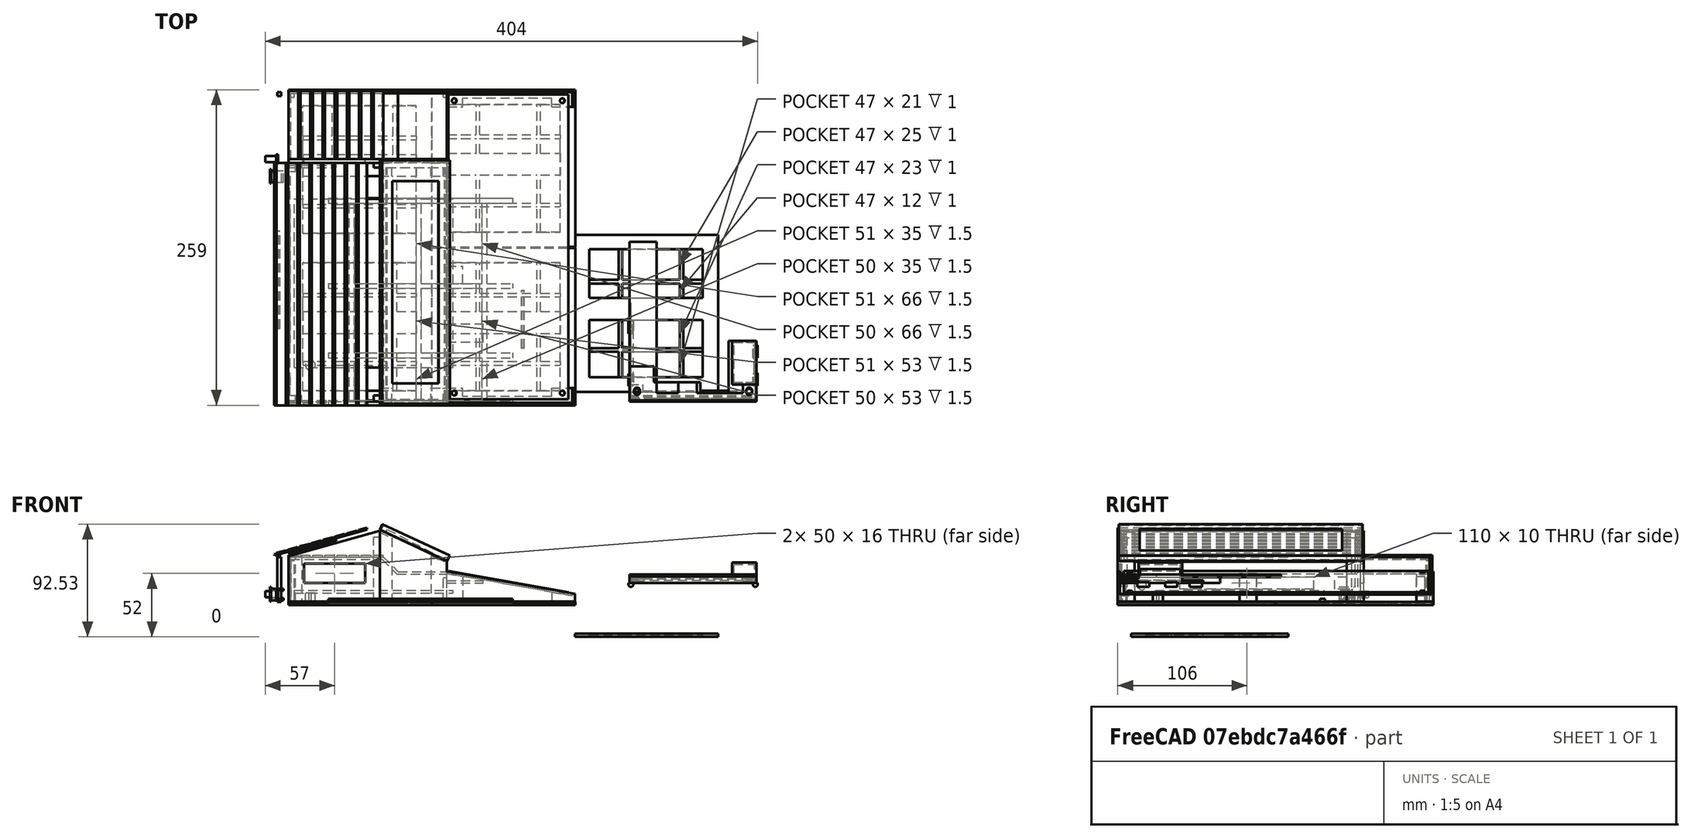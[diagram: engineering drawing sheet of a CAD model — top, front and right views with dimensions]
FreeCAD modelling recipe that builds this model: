
FCSTD DOCUMENT  (FreeCAD 0.20R29603 (Git))
Label: megav1
License: All rights reserved
LicenseURL: http://en.wikipedia.org/wiki/All_rights_reserved
objects: Part::Box×164, Part::Cut×62, Part::MultiFuse×26, Part::Cylinder×20, App::DocumentObjectGroup×8, Part::FeaturePython×1
note: 273 computed .brp shape members not serialized (recipe doc carries the construction recipe); baked Part::Feature solids carry a one-line shape summary decoded from their .brp

FEATURE [Part::Box] Box  label="5x50Keyboard"
  AttacherType = Attacher::AttachEngine3D
  Height = 2
  Length = 100
  Width = 250
FEATURE [Part::Box] Box001  label="MainBoardPCB"
  AttacherType = Attacher::AttachEngine3D
  Height = 2
  Length = 130
  Placement = pos=(-125,28,-8) rot=(0,0,1;0rad)
  Width = 138.5
FEATURE [Part::Box] Box002  label="4x40lcd"
  AttacherType = Attacher::AttachEngine3D
  Height = 2
  Length = 54
  Placement = pos=(-56,2,30) rot=(0,1,0;0.296706rad)
  Width = 190
FEATURE [Part::Box] Box050  label="Cube028"
  AttacherType = Attacher::AttachEngine3D
  Height = 9.5
  Length = 11
  Placement = pos=(0,0,35) rot=(0,0,1;0rad)
  Width = 9.5
FEATURE [Part::Box] Box051  label="Cube029"
  AttacherType = Attacher::AttachEngine3D
  Height = 12
  Length = 1
  Placement = pos=(0,-1,34) rot=(0,0,1;0rad)
  Width = 12
FEATURE [Part::Box] Box052  label="Cube030"
  AttacherType = Attacher::AttachEngine3D
  Height = 7.5
  Length = 4.5
  Placement = pos=(5,-1,36) rot=(0,0,1;0rad)
  Width = 13
FEATURE [Part::Box] Box053  label="Cube031"
  AttacherType = Attacher::AttachEngine3D
  Height = 6
  Length = 4.5
  Placement = pos=(9,-1,36.75) rot=(0,0,1;0rad)
  Width = 13
FEATURE [Part::Cylinder] Cylinder008
  Angle = 360
  AttacherType = Attacher::AttachEngine3D
  FirstAngle = 0
  Height = 9
  Placement = pos=(-1,5,40) rot=(0,1,0;1.5708rad)
  Radius = 3
  SecondAngle = 0
FEATURE [Part::MultiFuse] Fusion010
  Shapes = -> [Box050,Box051]
FEATURE [Part::Cut] Cut016
  Base = -> Fusion010
  Tool = -> Cylinder008
FEATURE [Part::Cut] Cut017
  Base = -> Cut016
  Tool = -> Box052
FEATURE [Part::Cut] Cut018
  Base = -> Cut017
  Placement = pos=(-145,180,-49) rot=(0,0,1;0rad)
  Tool = -> Box053
FEATURE [App::DocumentObjectGroup] Group007  label="resetbutton-case"
  Group = -> [Cut018]
FEATURE [Part::Box] Box054  label="Cube002"
  AttacherType = Attacher::AttachEngine3D
  Height = 37
  Length = 1.5
  Placement = pos=(0,0,-10) rot=(0,0,1;0rad)
  Width = 194
FEATURE [Part::Box] Box004  label="Cube003"
  AttacherType = Attacher::AttachEngine3D
  Height = 10
  Length = 10
  Placement = pos=(-3,48,0) rot=(0,0,1;0rad)
  Width = 110
FEATURE [Part::Box] Box021  label="reset"
  AttacherType = Attacher::AttachEngine3D
  Height = 10
  Length = 10
  Placement = pos=(-2,175,0) rot=(0,0,1;0rad)
  Width = 10
FEATURE [Part::Box] Box025  label="Cube004"
  AttacherType = Attacher::AttachEngine3D
  Height = 37
  Length = 5
  Placement = pos=(1,0,-8.5) rot=(0,0,1;0rad)
  Width = 5
FEATURE [Part::Box] Box026  label="Cube005"
  AttacherType = Attacher::AttachEngine3D
  Height = 37
  Length = 5
  Placement = pos=(1,189,-8.5) rot=(0,0,1;0rad)
  Width = 5
FEATURE [Part::Cylinder] Cylinder004  label="pwrjack"
  Angle = 360
  AttacherType = Attacher::AttachEngine3D
  FirstAngle = 0
  Height = 10
  Placement = pos=(-3,17,3) rot=(0,1,0;1.5708rad)
  Radius = 3.5
  SecondAngle = 0
FEATURE [Part::Cut] Cut003
  Base = -> Box054
  Tool = -> Cylinder004
FEATURE [Part::Cut] Cut
  Base = -> Cut003
  Tool = -> Box004
FEATURE [Part::Cut] Cut006
  Base = -> Cut
  Placement = pos=(0,0,1.5) rot=(0,0,1;0rad)
  Tool = -> Box021
FEATURE [Part::MultiFuse] Fusion011
  Placement = pos=(-130,0,-6.5) rot=(0,0,1;0rad)
  Shapes = -> [Box025,Cut006,Box026]
FEATURE [App::DocumentObjectGroup] Group002  label="Back"
  Group = -> [Fusion011]
FEATURE [Part::Box] Box055  label="Cube032"
  AttacherType = Attacher::AttachEngine3D
  Height = 5.5
  Length = 1.5
  Placement = pos=(7,1,37) rot=(0,0,1;0rad)
  Width = 8
FEATURE [Part::Cylinder] Cylinder009
  Angle = 360
  AttacherType = Attacher::AttachEngine3D
  FirstAngle = 0
  Height = 10
  Placement = pos=(-2,5,40) rot=(0,1,0;1.5708rad)
  Radius = 2.5
  SecondAngle = 0
FEATURE [Part::MultiFuse] Fusion012
  Placement = pos=(-147,194,-49) rot=(0,0,1;0rad)
  Shapes = -> [Cylinder009,Box055]
FEATURE [App::DocumentObjectGroup] Group008  label="resetbutton"
  Group = -> [Fusion012]
FEATURE [Part::Box] Box056  label="base"
  AttacherType = Attacher::AttachEngine3D
  Height = 1.5
  Length = 235
  Placement = pos=(-25,0,-10) rot=(1,0,0;0rad)
  Width = 259
FEATURE [Part::Box] Box027  label="Cube006"
  AttacherType = Attacher::AttachEngine3D
  Height = 4
  Length = 151
  Placement = pos=(8,0,-9) rot=(0,0,1;0rad)
  Width = 4
FEATURE [Part::Box] Box028  label="Cube007"
  AttacherType = Attacher::AttachEngine3D
  Height = 4
  Length = 151
  Placement = pos=(8,166,-9) rot=(0,0,1;0rad)
  Width = 4
FEATURE [Part::Box] Box029  label="Face003"
  AttacherType = Attacher::AttachEngine3D
  Height = 55
  Length = 2
  Placement = pos=(169.2,0,-11) rot=(0,-1,0;0.261799rad)
  Width = 254
FEATURE [Part::Box] Box036  label="Cube014"
  AttacherType = Attacher::AttachEngine3D
  Height = 2
  Length = 151
  Placement = pos=(8,96,-9) rot=(0,0,1;0rad)
  Width = 4
FEATURE [Part::Box] Box037  label="Cube015"
  AttacherType = Attacher::AttachEngine3D
  Height = 2
  Length = 151
  Placement = pos=(8,39,-9) rot=(0,0,1;0rad)
  Width = 4
FEATURE [Part::Box] Box038  label="Cube016"
  AttacherType = Attacher::AttachEngine3D
  Height = 2
  Length = 170
  Placement = pos=(29,0,-9) rot=(0,0,1;1.5708rad)
  Width = 4
FEATURE [Part::Box] Box039  label="Cube017"
  AttacherType = Attacher::AttachEngine3D
  Height = 2
  Length = 170
  Placement = pos=(84,0,-9) rot=(0,0,1;1.5708rad)
  Width = 4
FEATURE [Part::Box] Box040  label="Cube018"
  AttacherType = Attacher::AttachEngine3D
  Height = 2
  Length = 170
  Placement = pos=(138,0,-9) rot=(0,0,1;1.5708rad)
  Width = 4
FEATURE [Part::Cylinder] Cylinder007
  Angle = 360
  AttacherType = Attacher::AttachEngine3D
  FirstAngle = 0
  Height = 47
  Placement = pos=(167.4,94,-8.1) rot=(1,0,0;1.5708rad)
  Radius = 1
  SecondAngle = 0
FEATURE [Part::MultiFuse] Fusion005
  Shapes = -> [Box027,Box028]
FEATURE [Part::Cut] Cut009
  Base = -> Fusion005
  Tool = -> Box029
FEATURE [Part::MultiFuse] Fusion006
  Placement = pos=(-105,-3,-8) rot=(0,0,1;0rad)
  Refine = true
  Shapes = -> [Cut009,Cylinder007,Box036,Box037,Box038,Box039,Box040,Box056]
FEATURE [App::DocumentObjectGroup] Group009  label="CaseBaseold"
  Group = -> [Fusion006]
FEATURE [Part::FeaturePython] Tube002  label="PCBFoot"  # WARN: FeaturePython — macro-defined, semantics opaque (R4)
  AttacherType = Attacher::AttachEngine3D
  Height = 7
  InnerRadius = 1
  OuterRadius = 4
  Placement = pos=(-112,30,-15) rot=(0,0,1;0rad)
FEATURE [Part::Cylinder] Cylinder010
  Angle = 360
  AttacherType = Attacher::AttachEngine3D
  FirstAngle = 0
  Height = 20
  Placement = pos=(5,5,-2) rot=(0,0,1;0rad)
  Radius = 2
  SecondAngle = 0
FEATURE [Part::Cylinder] Cylinder011
  Angle = 360
  AttacherType = Attacher::AttachEngine3D
  FirstAngle = 0
  Height = 20
  Placement = pos=(5,245,-2) rot=(0,0,1;0rad)
  Radius = 2
  SecondAngle = 0
FEATURE [Part::Cylinder] Cylinder012
  Angle = 360
  AttacherType = Attacher::AttachEngine3D
  FirstAngle = 0
  Height = 20
  Placement = pos=(95,245,-2) rot=(0,0,1;0rad)
  Radius = 2
  SecondAngle = 0
FEATURE [Part::Cylinder] Cylinder013
  Angle = 360
  AttacherType = Attacher::AttachEngine3D
  FirstAngle = 0
  Height = 20
  Placement = pos=(95,5,-2) rot=(0,0,1;0rad)
  Radius = 2
  SecondAngle = 0
FEATURE [Part::Cut] Cut019
  Base = -> Box
  Tool = -> Cylinder010
FEATURE [Part::Cut] Cut020
  Base = -> Cut019
  Tool = -> Cylinder011
FEATURE [Part::Cut] Cut021
  Base = -> Cut020
  Tool = -> Cylinder012
FEATURE [Part::Cut] Cut022
  Base = -> Cut021
  Placement = pos=(0,2,5) rot=(0,0,1;0rad)
  Tool = -> Cylinder013
FEATURE [Part::MultiFuse] Fusion
  Placement = pos=(0,0,3) rot=(0,1,0;0.174533rad)
  Shapes = -> [Box002,Cut022]
FEATURE [App::DocumentObjectGroup] Group  label="PCB"
  Group = -> [Box001,Fusion]
FEATURE [Part::Box] Box057  label="pil1"
  AttacherType = Attacher::AttachEngine3D
  Height = 25
  Length = 105
  Placement = pos=(0,-2,-15) rot=(0,0,1;0rad)
  Width = 14
FEATURE [Part::Box] Box058  label="Cube033"
  AttacherType = Attacher::AttachEngine3D
  Height = 41
  Length = 116
  Placement = pos=(-1,-5,8) rot=(0,1,0;0.174533rad)
  Width = 17
FEATURE [Part::Cut] Cut023  label="leftpailslanted"
  Base = -> Box057
  Placement = pos=(0,-1,0) rot=(0,0,1;0rad)
  Tool = -> Box058
FEATURE [Part::Box] Box059  label="pil002"
  AttacherType = Attacher::AttachEngine3D
  Height = 25
  Length = 105
  Placement = pos=(0,-2,-15) rot=(0,0,1;0rad)
  Width = 2
FEATURE [Part::Box] Box060  label="Cube034"
  AttacherType = Attacher::AttachEngine3D
  Height = 41
  Length = 116
  Placement = pos=(-1,-5,8) rot=(0,1,0;0.174533rad)
  Width = 17
FEATURE [Part::Cut] Cut024  label="leftpailslanted001"
  Base = -> Box059
  Placement = pos=(0,-1,2) rot=(0,0,1;0rad)
  Tool = -> Box060
FEATURE [Part::Box] Box061  label="leftpilstop"
  AttacherType = Attacher::AttachEngine3D
  Height = 6
  Length = 2
  Placement = pos=(103,-3,-15) rot=(0,0,1;0rad)
  Width = 14
FEATURE [Part::Box] Box062  label="leftpilsfillremove"
  AttacherType = Attacher::AttachEngine3D
  Height = 27
  Length = 73
  Placement = pos=(13,4,-20) rot=(0,0,1;0rad)
  Width = 10
FEATURE [Part::Box] Box063  label="pil003"
  AttacherType = Attacher::AttachEngine3D
  Height = 25
  Length = 105
  Placement = pos=(0,-2,-15) rot=(0,0,1;0rad)
  Width = 14
FEATURE [Part::Box] Box064  label="Cube035"
  AttacherType = Attacher::AttachEngine3D
  Height = 41
  Length = 116
  Placement = pos=(-1,-5,8) rot=(0,1,0;0.174533rad)
  Width = 17
FEATURE [Part::Cut] Cut025  label="rightpailslanted001"
  Base = -> Box063
  Placement = pos=(0,-1,0) rot=(0,0,1;0rad)
  Tool = -> Box064
FEATURE [Part::Box] Box065  label="pil004"
  AttacherType = Attacher::AttachEngine3D
  Height = 25
  Length = 105
  Placement = pos=(0,-2,-15) rot=(0,0,1;0rad)
  Width = 2
FEATURE [Part::Box] Box066  label="Cube036"
  AttacherType = Attacher::AttachEngine3D
  Height = 41
  Length = 116
  Placement = pos=(-1,-5,8) rot=(0,1,0;0.174533rad)
  Width = 17
FEATURE [Part::Cut] Cut026  label="rightpailslanted002"
  Base = -> Box065
  Placement = pos=(0,11,2) rot=(0,0,1;0rad)
  Tool = -> Box066
FEATURE [Part::Box] Box067  label="rightpilstop001"
  AttacherType = Attacher::AttachEngine3D
  Height = 6
  Length = 2
  Placement = pos=(103,-3,-15) rot=(0,0,1;0rad)
  Width = 14
FEATURE [Part::Box] Box068  label="rightpilsfillremove001"
  AttacherType = Attacher::AttachEngine3D
  Height = 27
  Length = 73
  Placement = pos=(13,-6,-20) rot=(0,0,1;0rad)
  Width = 10
FEATURE [Part::MultiFuse] Fusion013
  Shapes = -> [Cut023,Cut024,Box061]
FEATURE [Part::Cut] Cut027  label="LeftPillar"
  Base = -> Fusion013
  Tool = -> Box062
FEATURE [Part::MultiFuse] Fusion014
  Shapes = -> [Cut025,Cut026,Box067]
FEATURE [Part::Cut] Cut028  label="keyboardrightpillar"
  Base = -> Fusion014
  Placement = pos=(0,245,0) rot=(0,0,1;0rad)
  Tool = -> Box068
FEATURE [Part::Box] Box069  label="lcdpillar"
  AttacherType = Attacher::AttachEngine3D
  Height = 58
  Length = 55
  Placement = pos=(-55,-3,-15) rot=(0,0,1;0rad)
  Width = 14
FEATURE [Part::Box] Box070  label="lcdpillar001slant"
  AttacherType = Attacher::AttachEngine3D
  Height = 58
  Length = 78
  Placement = pos=(-64,-6,48) rot=(0,1,0;0.436332rad)
  Width = 18
FEATURE [Part::Box] Box071  label="lcdpillar001slant001edge"
  AttacherType = Attacher::AttachEngine3D
  Height = 58
  Length = 78
  Placement = pos=(-64,-1,46) rot=(0,1,0;0.436332rad)
  Width = 18
FEATURE [Part::Cut] Cut029
  Base = -> Box069
  Tool = -> Box070
FEATURE [Part::Cut] Cut030
  Base = -> Cut029
  Tool = -> Box071
FEATURE [Part::Box] Box072  label="lcdstopleft"
  AttacherType = Attacher::AttachEngine3D
  Height = 9
  Length = 3
  Placement = pos=(-3,-3,10) rot=(0,0,1;0rad)
  Width = 14
FEATURE [Part::Box] Box073  label="lcdremove"
  AttacherType = Attacher::AttachEngine3D
  Height = 63
  Length = 32
  Placement = pos=(-45,-1,-17) rot=(0,0,1;0rad)
  Width = 17
FEATURE [Part::MultiFuse] Fusion015
  Shapes = -> [Cut030,Box072]
FEATURE [Part::Cut] Cut031  label="leftlcdpillar"
  Base = -> Fusion015
  Tool = -> Box073
FEATURE [Part::Box] Box080  label="lcdpillar002"
  AttacherType = Attacher::AttachEngine3D
  Height = 58
  Length = 55
  Placement = pos=(-55,-3,-15) rot=(0,0,1;0rad)
  Width = 14
FEATURE [Part::Box] Box081  label="lcdpillar001slant002"
  AttacherType = Attacher::AttachEngine3D
  Height = 58
  Length = 78
  Placement = pos=(-64,-6,48) rot=(0,1,0;0.436332rad)
  Width = 18
FEATURE [Part::Box] Box082  label="lcdpillar001slant001edge002"
  AttacherType = Attacher::AttachEngine3D
  Height = 58
  Length = 78
  Placement = pos=(-64,-10,46) rot=(0,1,0;0.436332rad)
  Width = 18
FEATURE [Part::Box] Box084  label="lcdremove002"
  AttacherType = Attacher::AttachEngine3D
  Height = 63
  Length = 32
  Placement = pos=(-45,-9,-17) rot=(0,0,1;0rad)
  Width = 17
FEATURE [Part::Cut] Cut035
  Base = -> Box080
  Tool = -> Box081
FEATURE [Part::Cut] Cut036
  Base = -> Cut035
  Tool = -> Box082
FEATURE [Part::MultiFuse] Fusion019  label="keyboardlcdleftpillar"
  Shapes = -> [Cut027,Cut031]
FEATURE [Part::Box] Box090  label="extcartslot"
  AttacherType = Attacher::AttachEngine3D
  Height = 61
  Length = 75
  Placement = pos=(-130,-3,-15) rot=(0,0,1;0rad)
  Width = 3
FEATURE [Part::Box] Box091  label="Cube039"
  AttacherType = Attacher::AttachEngine3D
  Height = 41
  Length = 107
  Placement = pos=(-150,-8,16.5) rot=(0,-1,0;0.272271rad)
  Width = 10
FEATURE [Part::Cut] Cut041
  Base = -> Box090
  Tool = -> Box091
FEATURE [Part::Box] Box092  label="Cube040"
  AttacherType = Attacher::AttachEngine3D
  Height = 53
  Length = 5
  Placement = pos=(-60,0,-15) rot=(0,0,1;0rad)
  Width = 5
FEATURE [Part::Box] Box093  label="Cube041"
  AttacherType = Attacher::AttachEngine3D
  Height = 37
  Length = 5
  Placement = pos=(-124,0,-15) rot=(0,0,1;0rad)
  Width = 5
FEATURE [Part::MultiFuse] Fusion021  label="LeftExtCartSlot"
  Shapes = -> [Cut041,Box092,Box093]
FEATURE [Part::Box] Box094  label="extcartslot001"
  AttacherType = Attacher::AttachEngine3D
  Height = 61
  Length = 75
  Placement = pos=(-130,-3,-15) rot=(0,0,1;0rad)
  Width = 3
FEATURE [Part::Box] Box095  label="Cube042"
  AttacherType = Attacher::AttachEngine3D
  Height = 41
  Length = 107
  Placement = pos=(-150,-8,16.5) rot=(0,-1,0;0.272271rad)
  Width = 10
FEATURE [Part::Box] Box096  label="Cube043"
  AttacherType = Attacher::AttachEngine3D
  Height = 53
  Length = 5
  Placement = pos=(-60,-7,-15) rot=(0,0,1;0rad)
  Width = 5
FEATURE [Part::Box] Box097  label="Cube044"
  AttacherType = Attacher::AttachEngine3D
  Height = 37
  Length = 5
  Placement = pos=(-124,-7,-15) rot=(0,0,1;0rad)
  Width = 5
FEATURE [Part::Cut] Cut042
  Base = -> Box094
  Tool = -> Box095
FEATURE [Part::MultiFuse] Fusion022  label="RightExtCartSlot001"
  Placement = pos=(0,209.01,0) rot=(0,0,1;0rad)
  Shapes = -> [Cut042,Box096,Box097]
FEATURE [Part::Box] Box098  label="Lid"
  AttacherType = Attacher::AttachEngine3D
  Height = 1.5
  Length = 79
  Placement = pos=(-130,-3,22) rot=(0,1,0;0rad)
  Width = 199
FEATURE [Part::Box] Box099  label="LidRib1"
  AttacherType = Attacher::AttachEngine3D
  Height = 1
  Length = 2
  Placement = pos=(-130,-3,61) rot=(0,-1,0;0rad)
  Width = 199
FEATURE [Part::Box] Box100  label="LidRib002"
  AttacherType = Attacher::AttachEngine3D
  Height = 1
  Length = 2
  Placement = pos=(-120,-3,61) rot=(0,-1,0;0rad)
  Width = 199
FEATURE [Part::Box] Box101  label="LidRib003"
  AttacherType = Attacher::AttachEngine3D
  Height = 1
  Length = 2
  Placement = pos=(-110,-3,61) rot=(0,-1,0;0rad)
  Width = 199
FEATURE [Part::Box] Box102  label="LidRib004"
  AttacherType = Attacher::AttachEngine3D
  Height = 1
  Length = 2
  Placement = pos=(-100,-3,61) rot=(0,-1,0;0rad)
  Width = 199
FEATURE [Part::Box] Box103  label="LidRib005"
  AttacherType = Attacher::AttachEngine3D
  Height = 1
  Length = 2
  Placement = pos=(-90,-3,61) rot=(0,-1,0;0rad)
  Width = 199
FEATURE [Part::Box] Box104  label="LidRib006"
  AttacherType = Attacher::AttachEngine3D
  Height = 1
  Length = 2
  Placement = pos=(-80,-3,61) rot=(0,-1,0;0rad)
  Width = 199
FEATURE [Part::Box] Box105  label="LidRib007"
  AttacherType = Attacher::AttachEngine3D
  Height = 1
  Length = 2
  Placement = pos=(-70,-3,61) rot=(0,-1,0;0rad)
  Width = 199
FEATURE [Part::Box] Box106  label="LidRib008"
  AttacherType = Attacher::AttachEngine3D
  Height = 1
  Length = 2
  Placement = pos=(-60,-3,61) rot=(0,-1,0;0rad)
  Width = 199
FEATURE [Part::Box] Box107  label="Cube045"
  AttacherType = Attacher::AttachEngine3D
  Height = 2
  Length = 40
  Placement = pos=(-118,-1,20) rot=(0,0,1;0rad)
  Width = 2
FEATURE [Part::Box] Box108  label="Cube046"
  AttacherType = Attacher::AttachEngine3D
  Height = 2
  Length = 40
  Placement = pos=(-118,192,20) rot=(0,0,1;0rad)
  Width = 2
FEATURE [Part::Box] Box109  label="Cube047"
  AttacherType = Attacher::AttachEngine3D
  Height = 2
  Length = 2
  Placement = pos=(-128,60,20) rot=(0,0,1;0rad)
  Width = 80
FEATURE [Part::MultiFuse] Fusion023  label="Lid001"
  Placement = pos=(0,0,38) rot=(0,1,0;0rad)
  Shapes = -> [Box098,Box107,Box108,Box109]
FEATURE [Part::Cut] Cut043
  Base = -> Fusion023
  Tool = -> Box099
FEATURE [Part::Cut] Cut044
  Base = -> Cut043
  Tool = -> Box100
FEATURE [Part::Cut] Cut045
  Base = -> Cut044
  Tool = -> Box101
FEATURE [Part::Cut] Cut046
  Base = -> Cut045
  Tool = -> Box102
FEATURE [Part::Cut] Cut047
  Base = -> Cut046
  Tool = -> Box103
FEATURE [Part::Cut] Cut048
  Base = -> Cut047
  Tool = -> Box104
FEATURE [Part::Cut] Cut049
  Base = -> Cut048
  Tool = -> Box105
FEATURE [Part::Cut] Cut050  label="Lid002"
  Base = -> Cut049
  Placement = pos=(0,0,0) rot=(0,-1,0;0.272271rad)
  Tool = -> Box106
FEATURE [Part::Box] Box110  label="Cube048"
  AttacherType = Attacher::AttachEngine3D
  Height = 16
  Length = 50
  Placement = pos=(-117,-8,0) rot=(0,0,1;0rad)
  Width = 10
FEATURE [Part::Cut] Cut051  label="LeftExtCartSlotWithHole"
  Base = -> Fusion021
  Tool = -> Box110
FEATURE [Part::Box] Box111  label="Cube049"
  AttacherType = Attacher::AttachEngine3D
  Height = 16
  Length = 50
  Placement = pos=(-117,203,0) rot=(0,0,1;0rad)
  Width = 10
FEATURE [Part::Cut] Cut052  label="RightExtCartSlotWithHole"
  Base = -> Fusion022
  Placement = pos=(0,-10,0) rot=(0,0,1;0rad)
  Tool = -> Box111
FEATURE [Part::Box] Box112  label="Cube050"
  AttacherType = Attacher::AttachEngine3D
  Height = 2
  Length = 104
  Placement = pos=(150,0,0) rot=(0,0,1;0rad)
  Width = 8
FEATURE [Part::Box] Box113  label="Cube051"
  AttacherType = Attacher::AttachEngine3D
  Height = 5.6
  Length = 104
  Placement = pos=(150,0,0) rot=(0,0,1;0rad)
  Width = 4
FEATURE [Part::Box] Box114  label="Cube052"
  AttacherType = Attacher::AttachEngine3D
  Height = 2
  Length = 104
  Placement = pos=(150,0,3.6) rot=(0,0,1;0rad)
  Width = 8
FEATURE [Part::Box] Box115  label="Cube053"
  AttacherType = Attacher::AttachEngine3D
  Height = 2
  Length = 11
  Placement = pos=(150,4,0) rot=(0,0,1;0rad)
  Width = 10
FEATURE [Part::Cylinder] Cylinder
  Angle = 360
  AttacherType = Attacher::AttachEngine3D
  FirstAngle = 0
  Height = 10
  Placement = pos=(156,9,-3) rot=(0,0,1;0rad)
  Radius = 2.5
  SecondAngle = 0
FEATURE [Part::Box] Box116  label="Cube054"
  AttacherType = Attacher::AttachEngine3D
  Height = 2
  Length = 11
  Placement = pos=(150,4,3.6) rot=(0,0,1;0rad)
  Width = 10
FEATURE [Part::Box] Box117  label="Cube055"
  AttacherType = Attacher::AttachEngine3D
  Height = 2
  Length = 11
  Placement = pos=(243,4,3.6) rot=(0,0,1;0rad)
  Width = 10
FEATURE [Part::Box] Box118  label="Cube056"
  AttacherType = Attacher::AttachEngine3D
  Height = 2
  Length = 11
  Placement = pos=(243,4,0) rot=(0,0,1;0rad)
  Width = 10
FEATURE [Part::Cylinder] Cylinder014
  Angle = 360
  AttacherType = Attacher::AttachEngine3D
  FirstAngle = 0
  Height = 10
  Placement = pos=(248,9,-3) rot=(0,0,1;0rad)
  Radius = 2.5
  SecondAngle = 0
FEATURE [Part::MultiFuse] Fusion024
  Shapes = -> [Box112,Box113,Box114,Box115,Box116,Box117,Box118]
FEATURE [Part::Cut] Cut053
  Base = -> Fusion024
  Tool = -> Cylinder014
FEATURE [Part::Cut] Cut054  label="KeyBoardRiser"
  Base = -> Cut053
  Tool = -> Cylinder
FEATURE [Part::Box] Box083  label="lcdstopleft002"
  AttacherType = Attacher::AttachEngine3D
  Height = 9
  Length = 3
  Placement = pos=(-3,-3,10) rot=(0,0,1;0rad)
  Width = 14
FEATURE [Part::MultiFuse] Fusion017
  Shapes = -> [Cut036,Box083]
FEATURE [Part::Cut] Cut037  label="rightlcdpillar002"
  Base = -> Fusion017
  Placement = pos=(0,188,0) rot=(0,0,1;0rad)
  Tool = -> Box084
FEATURE [Part::Box] Box143  label="NewBasePanel008"
  AttacherType = Attacher::AttachEngine3D
  Height = 2.5
  Length = 117.5
  Placement = pos=(105,8,-45) rot=(0,0,1;0rad)
  Width = 129
FEATURE [Part::Box] Box144  label="NewBasePanel009"
  AttacherType = Attacher::AttachEngine3D
  Height = 2.5
  Length = 93
  Placement = pos=(117,20,-44) rot=(0,0,1;0rad)
  Width = 105
FEATURE [Part::Box] Box145  label="Cube072"
  AttacherType = Attacher::AttachEngine3D
  Height = 1
  Length = 116.5
  Placement = pos=(105,41,-43) rot=(0,0,1;0rad)
  Width = 3
FEATURE [Part::Box] Box146  label="Cube073"
  AttacherType = Attacher::AttachEngine3D
  Height = 1
  Length = 116.5
  Placement = pos=(105,97,-43) rot=(0,0,1;0rad)
  Width = 3
FEATURE [Part::Box] Box147  label="Cube074"
  AttacherType = Attacher::AttachEngine3D
  Height = 1
  Length = 3
  Placement = pos=(141,8,-43) rot=(0,0,1;0rad)
  Width = 129
FEATURE [Part::Box] Box148  label="Cube075"
  AttacherType = Attacher::AttachEngine3D
  Height = 1
  Length = 3
  Placement = pos=(191,8,-43) rot=(0,0,1;0rad)
  Width = 129
FEATURE [Part::Cut] Cut059
  Base = -> Box143
  Placement = pos=(0,0,1) rot=(0,0,1;0rad)
  Tool = -> Box144
FEATURE [Part::Box] Box149  label="Cube076"
  AttacherType = Attacher::AttachEngine3D
  Height = 1.5
  Length = 116.5
  Placement = pos=(105,67,-43) rot=(0,0,1;0rad)
  Width = 18
FEATURE [Part::MultiFuse] Fusion029  label="NewBasePanelSection"
  Shapes = -> [Cut059,Box145,Box146,Box147,Box148,Box149]
FEATURE [Part::Box] Box178  label="NewBasePanel018"
  AttacherType = Attacher::AttachEngine3D
  Height = 2.5
  Length = 117.5
  Placement = pos=(105,8,-45) rot=(0,0,1;0rad)
  Width = 129
FEATURE [Part::Box] Box179  label="NewBasePanel019"
  AttacherType = Attacher::AttachEngine3D
  Height = 2.5
  Length = 93
  Placement = pos=(117,20,-44) rot=(0,0,1;0rad)
  Width = 105
FEATURE [Part::Box] Box180  label="Cube097"
  AttacherType = Attacher::AttachEngine3D
  Height = 1
  Length = 116.5
  Placement = pos=(105,41,-43) rot=(0,0,1;0rad)
  Width = 3
FEATURE [Part::Box] Box181  label="Cube098"
  AttacherType = Attacher::AttachEngine3D
  Height = 1
  Length = 116.5
  Placement = pos=(105,97,-43) rot=(0,0,1;0rad)
  Width = 3
FEATURE [Part::Box] Box182  label="Cube099"
  AttacherType = Attacher::AttachEngine3D
  Height = 1
  Length = 3
  Placement = pos=(141,8,-43) rot=(0,0,1;0rad)
  Width = 129
FEATURE [Part::Box] Box183  label="Cube100"
  AttacherType = Attacher::AttachEngine3D
  Height = 1
  Length = 3
  Placement = pos=(191,8,-43) rot=(0,0,1;0rad)
  Width = 129
FEATURE [Part::Box] Box184  label="Cube101"
  AttacherType = Attacher::AttachEngine3D
  Height = 1
  Length = 116.5
  Placement = pos=(105,67,-43) rot=(0,0,1;0rad)
  Width = 18
FEATURE [Part::Cut] Cut064
  Base = -> Box178
  Placement = pos=(0,0,1) rot=(0,0,1;0rad)
  Tool = -> Box179
FEATURE [Part::MultiFuse] Fusion035  label="NewBasePanelSection005"
  Shapes = -> [Cut064,Box180,Box181,Box182,Box183,Box184]
FEATURE [Part::Box] Box185  label="NewBasePanel020"
  AttacherType = Attacher::AttachEngine3D
  Height = 2.5
  Length = 117.5
  Placement = pos=(105,8,-45) rot=(0,0,1;0rad)
  Width = 129
FEATURE [Part::Box] Box186  label="NewBasePanel021"
  AttacherType = Attacher::AttachEngine3D
  Height = 2.5
  Length = 93
  Placement = pos=(117,20,-44) rot=(0,0,1;0rad)
  Width = 105
FEATURE [Part::Box] Box187  label="Cube102"
  AttacherType = Attacher::AttachEngine3D
  Height = 1
  Length = 116.5
  Placement = pos=(105,41,-43) rot=(0,0,1;0rad)
  Width = 3
FEATURE [Part::Box] Box188  label="Cube103"
  AttacherType = Attacher::AttachEngine3D
  Height = 1
  Length = 116.5
  Placement = pos=(105,97,-43) rot=(0,0,1;0rad)
  Width = 3
FEATURE [Part::Box] Box189  label="Cube104"
  AttacherType = Attacher::AttachEngine3D
  Height = 1
  Length = 3
  Placement = pos=(141,8,-43) rot=(0,0,1;0rad)
  Width = 129
FEATURE [Part::Box] Box190  label="Cube105"
  AttacherType = Attacher::AttachEngine3D
  Height = 1
  Length = 3
  Placement = pos=(191,8,-43) rot=(0,0,1;0rad)
  Width = 129
FEATURE [Part::Box] Box191  label="Cube106"
  AttacherType = Attacher::AttachEngine3D
  Height = 1
  Length = 116.5
  Placement = pos=(105,67,-43) rot=(0,0,1;0rad)
  Width = 18
FEATURE [Part::Cut] Cut065
  Base = -> Box185
  Placement = pos=(0,0,1) rot=(0,0,1;0rad)
  Tool = -> Box186
FEATURE [Part::MultiFuse] Fusion036  label="NewBasePanelSection006"
  Placement = pos=(-118,0,0) rot=(0,0,1;0rad)
  Shapes = -> [Cut065,Box187,Box188,Box189,Box190,Box191]
FEATURE [Part::Box] Box192  label="NewBasePanel022"
  AttacherType = Attacher::AttachEngine3D
  Height = 2.5
  Length = 117.5
  Placement = pos=(105,8,-45) rot=(0,0,1;0rad)
  Width = 129
FEATURE [Part::Box] Box193  label="NewBasePanel023"
  AttacherType = Attacher::AttachEngine3D
  Height = 2.5
  Length = 93
  Placement = pos=(117,20,-44) rot=(0,0,1;0rad)
  Width = 105
FEATURE [Part::Box] Box194  label="Cube107"
  AttacherType = Attacher::AttachEngine3D
  Height = 1
  Length = 116.5
  Placement = pos=(105,41,-43) rot=(0,0,1;0rad)
  Width = 3
FEATURE [Part::Box] Box195  label="Cube108"
  AttacherType = Attacher::AttachEngine3D
  Height = 1
  Length = 116.5
  Placement = pos=(105,97,-43) rot=(0,0,1;0rad)
  Width = 3
FEATURE [Part::Box] Box196  label="Cube109"
  AttacherType = Attacher::AttachEngine3D
  Height = 1
  Length = 3
  Placement = pos=(141,8,-43) rot=(0,0,1;0rad)
  Width = 129
FEATURE [Part::Box] Box197  label="Cube110"
  AttacherType = Attacher::AttachEngine3D
  Height = 1
  Length = 3
  Placement = pos=(191,8,-43) rot=(0,0,1;0rad)
  Width = 129
FEATURE [Part::Box] Box198  label="Cube111"
  AttacherType = Attacher::AttachEngine3D
  Height = 1
  Length = 116.5
  Placement = pos=(105,67,-43) rot=(0,0,1;0rad)
  Width = 18
FEATURE [Part::Cut] Cut066
  Base = -> Box192
  Placement = pos=(0,0,1) rot=(0,0,1;0rad)
  Tool = -> Box193
FEATURE [Part::MultiFuse] Fusion037  label="NewBasePanelSection007"
  Placement = pos=(-118,129,0) rot=(0,0,1;0rad)
  Shapes = -> [Cut066,Box194,Box195,Box196,Box197,Box198]
FEATURE [Part::Box] Box199  label="NewBasePanel024"
  AttacherType = Attacher::AttachEngine3D
  Height = 2.5
  Length = 117.5
  Placement = pos=(105,8,-45) rot=(0,0,1;0rad)
  Width = 129
FEATURE [Part::Box] Box200  label="NewBasePanel025"
  AttacherType = Attacher::AttachEngine3D
  Height = 2.5
  Length = 93
  Placement = pos=(117,20,-44) rot=(0,0,1;0rad)
  Width = 105
FEATURE [Part::Box] Box201  label="Cube112"
  AttacherType = Attacher::AttachEngine3D
  Height = 1
  Length = 116.5
  Placement = pos=(105,41,-43) rot=(0,0,1;0rad)
  Width = 3
FEATURE [Part::Box] Box202  label="Cube113"
  AttacherType = Attacher::AttachEngine3D
  Height = 1
  Length = 116.5
  Placement = pos=(105,97,-43) rot=(0,0,1;0rad)
  Width = 3
FEATURE [Part::Box] Box203  label="Cube114"
  AttacherType = Attacher::AttachEngine3D
  Height = 1
  Length = 3
  Placement = pos=(141,8,-43) rot=(0,0,1;0rad)
  Width = 129
FEATURE [Part::Box] Box204  label="Cube115"
  AttacherType = Attacher::AttachEngine3D
  Height = 1
  Length = 3
  Placement = pos=(191,8,-43) rot=(0,0,1;0rad)
  Width = 129
FEATURE [Part::Box] Box205  label="Cube116"
  AttacherType = Attacher::AttachEngine3D
  Height = 1
  Length = 116.5
  Placement = pos=(105,67,-43) rot=(0,0,1;0rad)
  Width = 18
FEATURE [Part::Cut] Cut067
  Base = -> Box199
  Placement = pos=(0,0,1) rot=(0,0,1;0rad)
  Tool = -> Box200
FEATURE [Part::MultiFuse] Fusion038  label="NewBasePanelSection008"
  Placement = pos=(0,130,0) rot=(0,0,1;0rad)
  Shapes = -> [Cut067,Box201,Box202,Box203,Box204,Box205]
FEATURE [Part::MultiFuse] Fusion030
  Placement = pos=(-117,-11,26) rot=(0,0,1;0rad)
  Shapes = -> [Fusion036,Fusion037,Fusion038,Fusion035]
FEATURE [App::DocumentObjectGroup] Group011  label="NewBase"
  Group = -> [Fusion030]
FEATURE [Part::Box] Box206  label="pil005"
  AttacherType = Attacher::AttachEngine3D
  Height = 25
  Length = 105
  Placement = pos=(0,-2,-15) rot=(0,0,1;0rad)
  Width = 14
FEATURE [Part::Box] Box207  label="Cube117"
  AttacherType = Attacher::AttachEngine3D
  Height = 41
  Length = 116
  Placement = pos=(-1,-5,8) rot=(0,1,0;0.174533rad)
  Width = 17
FEATURE [Part::Cut] Cut068  label="rightpailslanted003"
  Base = -> Box206
  Placement = pos=(0,99,0) rot=(0,0,1;0rad)
  Tool = -> Box207
FEATURE [Part::Box] Box208  label="Cube"
  AttacherType = Attacher::AttachEngine3D
  Height = 25
  Length = 120
  Placement = pos=(13,95,-18) rot=(0,0,1;0rad)
  Width = 23
FEATURE [Part::Cut] Cut069  label="keyboardcentrepillar"
  Base = -> Cut068
  Tool = -> Box208
FEATURE [App::DocumentObjectGroup] Group010  label="KeyboardPillars"
  Group = -> [Fusion019,Cut037,Cut028,Cut069]
FEATURE [Part::Box] Box209  label="LinkPlate"
  AttacherType = Attacher::AttachEngine3D
  Height = 2
  Length = 30
  Placement = pos=(0,49,0) rot=(0,0,1;0rad)
  Width = 15
FEATURE [Part::Box] Box210  label="Cube118"
  AttacherType = Attacher::AttachEngine3D
  Height = 37
  Length = 130
  Placement = pos=(-40,201,9.5) rot=(0,-1,0;0.785398rad)
  Width = 54
FEATURE [Part::Box] Box211  label="Cube119"
  AttacherType = Attacher::AttachEngine3D
  Height = 37
  Length = 130
  Placement = pos=(-130,201,-15.5) rot=(0,0,1;0rad)
  Width = 2
FEATURE [Part::Box] Box212  label="Cube120"
  AttacherType = Attacher::AttachEngine3D
  Height = 37
  Length = 130
  Placement = pos=(-40,201,9.5) rot=(0,0,1;0rad)
  Width = 54
FEATURE [Part::Cut] Cut070
  Base = -> Box211
  Tool = -> Box210
FEATURE [Part::Cut] Cut071  label="BoxPanel"
  Base = -> Cut070
  Placement = pos=(0,53,0) rot=(0,0,1;0rad)
  Tool = -> Box212
FEATURE [Part::Box] Box213  label="Cube121"
  AttacherType = Attacher::AttachEngine3D
  Height = 20
  Length = 3
  Placement = pos=(-3,251,-15.5) rot=(0,0,1;0rad)
  Width = 3
FEATURE [Part::Box] Box214  label="Cube122"
  AttacherType = Attacher::AttachEngine3D
  Height = 34
  Length = 3
  Placement = pos=(-128,251,-15.5) rot=(0,0,1;0rad)
  Width = 3
FEATURE [Part::Box] Box215  label="BoxPanelSupports"
  AttacherType = Attacher::AttachEngine3D
  Height = 37
  Length = 3
  Placement = pos=(-139,251,-15.5) rot=(0,0,1;0rad)
  Width = 3
FEATURE [Part::MultiFuse] Fusion039  label="BoxPanelRight"
  Placement = pos=(0,-1,0) rot=(0,0,1;0rad)
  Shapes = -> [Cut071,Box213,Box214]
FEATURE [Part::Box] Box216  label="Cube123"
  AttacherType = Attacher::AttachEngine3D
  Height = 37
  Length = 130
  Placement = pos=(-130,199,-15.5) rot=(0,0,1;0rad)
  Width = 54
FEATURE [Part::Box] Box217  label="Cube124"
  AttacherType = Attacher::AttachEngine3D
  Height = 36
  Length = 128
  Placement = pos=(-40,199,9.5) rot=(0,-1,0;0.785398rad)
  Width = 58
FEATURE [Part::Box] Box218  label="Cube125"
  AttacherType = Attacher::AttachEngine3D
  Height = 37
  Length = 75
  Placement = pos=(-128,199,-17.5) rot=(0,0,1;0rad)
  Width = 63
FEATURE [Part::Box] Box219  label="Cube126"
  AttacherType = Attacher::AttachEngine3D
  Height = 36
  Length = 128
  Placement = pos=(-118,198,-96.5) rot=(0,-1,0;0.785398rad)
  Width = 60
FEATURE [Part::Cut] Cut072
  Base = -> Box216
  Tool = -> Box217
FEATURE [Part::Cut] Cut073
  Base = -> Cut072
  Tool = -> Box218
FEATURE [Part::Cut] Cut074
  Base = -> Cut073
  Tool = -> Box219
FEATURE [Part::Box] Box220  label="Cube127"
  AttacherType = Attacher::AttachEngine3D
  Height = 37
  Length = 75
  Placement = pos=(-75,199,-29.5) rot=(0,0,1;0rad)
  Width = 63
FEATURE [Part::Box] Box221  label="Cube128"
  AttacherType = Attacher::AttachEngine3D
  Height = 37
  Length = 75
  Placement = pos=(-40,199,9.5) rot=(0,0,1;0rad)
  Width = 63
FEATURE [Part::Cut] Cut075
  Base = -> Cut074
  Tool = -> Box220
FEATURE [Part::Cut] Cut076  label="BoxLidShape"
  Base = -> Cut075
  Tool = -> Box221
FEATURE [Part::Box] Box222  label="BoxPanelSupports001"
  AttacherType = Attacher::AttachEngine3D
  Height = 56
  Length = 8
  Placement = pos=(-130,255,21.5) rot=(1,0,0;1.5708rad)
  Width = 1.5
FEATURE [Part::Box] Box223  label="BoxPanelSupports002"
  AttacherType = Attacher::AttachEngine3D
  Height = 56
  Length = 8
  Placement = pos=(-120,255,21.5) rot=(1,0,0;1.5708rad)
  Width = 1.5
FEATURE [Part::Box] Box224  label="BoxPanelSupports003"
  AttacherType = Attacher::AttachEngine3D
  Height = 56
  Length = 8
  Placement = pos=(-110,255,21.5) rot=(1,0,0;1.5708rad)
  Width = 1.5
FEATURE [Part::Box] Box225  label="BoxPanelSupports004"
  AttacherType = Attacher::AttachEngine3D
  Height = 56
  Length = 8
  Placement = pos=(-60,255,21.5) rot=(1,0,0;1.5708rad)
  Width = 1.5
FEATURE [Part::Box] Box226  label="BoxPanelSupports005"
  AttacherType = Attacher::AttachEngine3D
  Height = 56
  Length = 8
  Placement = pos=(-100,255,21.5) rot=(1,0,0;1.5708rad)
  Width = 1.5
FEATURE [Part::Box] Box227  label="BoxPanelSupports006"
  AttacherType = Attacher::AttachEngine3D
  Height = 56
  Length = 8
  Placement = pos=(-90,255,21.5) rot=(1,0,0;1.5708rad)
  Width = 1.5
FEATURE [Part::Box] Box228  label="BoxPanelSupports007"
  AttacherType = Attacher::AttachEngine3D
  Height = 56
  Length = 8
  Placement = pos=(-80,255,21.5) rot=(1,0,0;1.5708rad)
  Width = 1.5
FEATURE [Part::Box] Box229  label="BoxPanelSupports008"
  AttacherType = Attacher::AttachEngine3D
  Height = 56
  Length = 8
  Placement = pos=(-70,255,21.5) rot=(1,0,0;1.5708rad)
  Width = 1.5
FEATURE [Part::MultiFuse] Fusion040  label="BoxLid"
  Shapes = -> [Cut076,Box222,Box223,Box224,Box225,Box227,Box226,Box228,Box229]
FEATURE [Part::Box] Box232  label="lcdbezelouter"
  AttacherType = Attacher::AttachEngine3D
  Height = 5
  Length = 61
  Placement = pos=(-55,-2,44) rot=(0,1,0;0.436332rad)
  Width = 200
FEATURE [Part::Box] Box233  label="Cube129"
  AttacherType = Attacher::AttachEngine3D
  Height = 10
  Length = 42
  Placement = pos=(-46,15,42) rot=(0,1,0;0.436332rad)
  Width = 166
FEATURE [Part::Cut] Cut077
  Base = -> Box232
  Tool = -> Box233
FEATURE [Part::Box] Box234  label="lcdbezelouter001"
  AttacherType = Attacher::AttachEngine3D
  Height = 5
  Length = 59
  Placement = pos=(-54,-1,43) rot=(0,1,0;0.436332rad)
  Width = 198
FEATURE [Part::Cut] Cut078  label="LcdBezel"
  Base = -> Cut077
  Tool = -> Box234
FEATURE [Part::Box] Box235  label="Cube130"
  AttacherType = Attacher::AttachEngine3D
  Height = 2
  Length = 104
  Placement = pos=(150,1,0) rot=(0,0,1;0rad)
  Width = 8
FEATURE [Part::Box] Box236  label="Cube131"
  AttacherType = Attacher::AttachEngine3D
  Height = 5.6
  Length = 104
  Placement = pos=(150,1,0) rot=(0,0,1;0rad)
  Width = 4
FEATURE [Part::Box] Box237  label="Cube132"
  AttacherType = Attacher::AttachEngine3D
  Height = 2
  Length = 104
  Placement = pos=(150,1,3.6) rot=(0,0,1;0rad)
  Width = 8
FEATURE [Part::Box] Box238  label="Cube133"
  AttacherType = Attacher::AttachEngine3D
  Height = 2
  Length = 11
  Placement = pos=(150,4,0) rot=(0,0,1;0rad)
  Width = 10
FEATURE [Part::Box] Box239  label="Cube134"
  AttacherType = Attacher::AttachEngine3D
  Height = 2
  Length = 11
  Placement = pos=(150,4,3.6) rot=(0,0,1;0rad)
  Width = 10
FEATURE [Part::Box] Box240  label="Cube135"
  AttacherType = Attacher::AttachEngine3D
  Height = 2
  Length = 11
  Placement = pos=(243,4,3.6) rot=(0,0,1;0rad)
  Width = 10
FEATURE [Part::Box] Box241  label="Cube136"
  AttacherType = Attacher::AttachEngine3D
  Height = 2
  Length = 11
  Placement = pos=(243,4,0) rot=(0,0,1;0rad)
  Width = 10
FEATURE [Part::Cylinder] Cylinder015
  Angle = 360
  AttacherType = Attacher::AttachEngine3D
  FirstAngle = 0
  Height = 10
  Placement = pos=(156,9,-3) rot=(0,0,1;0rad)
  Radius = 2.5
  SecondAngle = 0
FEATURE [Part::Cylinder] Cylinder016
  Angle = 360
  AttacherType = Attacher::AttachEngine3D
  FirstAngle = 0
  Height = 10
  Placement = pos=(248,9,-3) rot=(0,0,1;0rad)
  Radius = 2.5
  SecondAngle = 0
FEATURE [Part::MultiFuse] Fusion041
  Shapes = -> [Box235,Box236,Box237,Box238,Box239,Box240,Box241]
FEATURE [Part::Cut] Cut079
  Base = -> Fusion041
  Tool = -> Cylinder016
FEATURE [Part::Cut] Cut080  label="KeyBoardRiser001"
  Base = -> Cut079
  Tool = -> Cylinder015
FEATURE [Part::Box] Box243  label="Cube138"
  AttacherType = Attacher::AttachEngine3D
  Height = 7
  Length = 104
  Placement = pos=(150,1,0) rot=(0,0,1;0rad)
  Width = 2
FEATURE [Part::Box] Box244  label="Cube139"
  AttacherType = Attacher::AttachEngine3D
  Height = 2
  Length = 104
  Placement = pos=(150,1,5) rot=(0,0,1;0rad)
  Width = 6
FEATURE [Part::Box] Box246  label="Cube141"
  AttacherType = Attacher::AttachEngine3D
  Height = 2
  Length = 11
  Placement = pos=(150,4,5) rot=(0,0,1;0rad)
  Width = 10
FEATURE [Part::Box] Box247  label="Cube142"
  AttacherType = Attacher::AttachEngine3D
  Height = 2
  Length = 11
  Placement = pos=(243,4,5) rot=(0,0,1;0rad)
  Width = 10
FEATURE [Part::Cylinder] Cylinder017
  Angle = 360
  AttacherType = Attacher::AttachEngine3D
  FirstAngle = 0
  Height = 10
  Placement = pos=(156,9,-3) rot=(0,0,1;0rad)
  Radius = 2.5
  SecondAngle = 0
FEATURE [Part::Cylinder] Cylinder018
  Angle = 360
  AttacherType = Attacher::AttachEngine3D
  FirstAngle = 0
  Height = 10
  Placement = pos=(248,9,-3) rot=(0,0,1;0rad)
  Radius = 2.5
  SecondAngle = 0
FEATURE [Part::Box] Box248  label="Cube143"
  AttacherType = Attacher::AttachEngine3D
  Height = 2
  Length = 22
  Placement = pos=(150,1,5) rot=(0,0,1;0rad)
  Width = 130
FEATURE [Part::Box] Box249  label="Cube144"
  AttacherType = Attacher::AttachEngine3D
  Height = 2
  Length = 15
  Placement = pos=(190,1,5) rot=(0,0,1;0rad)
  Width = 15
FEATURE [Part::Box] Box250  label="Cube145"
  AttacherType = Attacher::AttachEngine3D
  Height = 7
  Length = 1
  Placement = pos=(150,1,0) rot=(0,0,1;0rad)
  Width = 80
FEATURE [Part::Box] Box251  label="Cube146"
  AttacherType = Attacher::AttachEngine3D
  Height = 2
  Length = 2
  Placement = pos=(151,17,0.4) rot=(0,0,1;0rad)
  Width = 50
FEATURE [Part::Cylinder] Cylinder019
  Angle = 360
  AttacherType = Attacher::AttachEngine3D
  FirstAngle = 0
  Height = 10
  Placement = pos=(151,23,-1) rot=(1,0,0;1.5708rad)
  Radius = 2
  SecondAngle = 0
FEATURE [Part::Cylinder] Cylinder020
  Angle = 360
  AttacherType = Attacher::AttachEngine3D
  FirstAngle = 0
  Height = 10
  Placement = pos=(151,66,-1) rot=(1,0,0;1.5708rad)
  Radius = 2
  SecondAngle = 0
FEATURE [Part::MultiFuse] Fusion042
  Shapes = -> [Box243,Box244,Box246,Box247,Box248,Box249,Box250,Box251,Cylinder019,Cylinder020]
FEATURE [Part::Cut] Cut081
  Base = -> Fusion042
  Tool = -> Cylinder018
FEATURE [Part::Cut] Cut082  label="KeyboardBezelLeft"
  Base = -> Cut081
  Tool = -> Cylinder017
FEATURE [Part::Box] Box268  label="Cube163"
  AttacherType = Attacher::AttachEngine3D
  Height = 7
  Length = 104
  Placement = pos=(150,1,0) rot=(0,0,1;0rad)
  Width = 2
FEATURE [Part::Box] Box269  label="Cube164"
  AttacherType = Attacher::AttachEngine3D
  Height = 2
  Length = 104
  Placement = pos=(150,1,5) rot=(0,0,1;0rad)
  Width = 6
FEATURE [Part::Box] Box270  label="Cube165"
  AttacherType = Attacher::AttachEngine3D
  Height = 2
  Length = 11
  Placement = pos=(150,4,5) rot=(0,0,1;0rad)
  Width = 10
FEATURE [Part::Box] Box271  label="Cube166"
  AttacherType = Attacher::AttachEngine3D
  Height = 2
  Length = 11
  Placement = pos=(243,4,5) rot=(0,0,1;0rad)
  Width = 10
FEATURE [Part::Box] Box272  label="Cube167"
  AttacherType = Attacher::AttachEngine3D
  Height = 10
  Length = 20
  Placement = pos=(234,13,7) rot=(0,0,1;0rad)
  Width = 36
FEATURE [Part::Box] Box273  label="Cube168"
  AttacherType = Attacher::AttachEngine3D
  Height = 2
  Length = 57
  Placement = pos=(151,1,5) rot=(0,0,1;0rad)
  Width = 15
FEATURE [Part::Box] Box274  label="Cube169"
  AttacherType = Attacher::AttachEngine3D
  Height = 7
  Length = 1
  Placement = pos=(253,1,0) rot=(0,0,1;0rad)
  Width = 49
FEATURE [Part::Box] Box275  label="Cube170"
  AttacherType = Attacher::AttachEngine3D
  Height = 2
  Length = 2
  Placement = pos=(252,13,0.4) rot=(0,0,1;0rad)
  Width = 32
FEATURE [Part::Cylinder] Cylinder029
  Angle = 360
  AttacherType = Attacher::AttachEngine3D
  FirstAngle = 0
  Height = 10
  Placement = pos=(156,8,-3) rot=(0,0,1;0rad)
  Radius = 2.5
  SecondAngle = 0
FEATURE [Part::Cylinder] Cylinder030
  Angle = 360
  AttacherType = Attacher::AttachEngine3D
  FirstAngle = 0
  Height = 10
  Placement = pos=(248,8,-3) rot=(0,0,1;0rad)
  Radius = 2.5
  SecondAngle = 0
FEATURE [Part::Cylinder] Cylinder031
  Angle = 360
  AttacherType = Attacher::AttachEngine3D
  FirstAngle = 0
  Height = 10
  Placement = pos=(253,23,-1) rot=(1,0,0;1.5708rad)
  Radius = 2
  SecondAngle = 0
FEATURE [Part::Cylinder] Cylinder032
  Angle = 360
  AttacherType = Attacher::AttachEngine3D
  FirstAngle = 0
  Height = 10
  Placement = pos=(253,46,-1) rot=(1,0,0;1.5708rad)
  Radius = 2
  SecondAngle = 0
FEATURE [Part::Box] Box276  label="Cube171"
  AttacherType = Attacher::AttachEngine3D
  Height = 2
  Length = 20
  Placement = pos=(150,1,5) rot=(0,0,1;0rad)
  Width = 28
FEATURE [Part::Box] Box277  label="Cube172"
  AttacherType = Attacher::AttachEngine3D
  Height = 2
  Length = 22
  Placement = pos=(231,1,5) rot=(0,0,1;0rad)
  Width = 13
FEATURE [Part::Box] Box278  label="Cube173"
  AttacherType = Attacher::AttachEngine3D
  Height = 12
  Length = 17
  Placement = pos=(235.5,14.5,3.5) rot=(0,0,1;0rad)
  Width = 33
FEATURE [Part::Cut] Cut087
  Base = -> Box272
  Tool = -> Box278
FEATURE [Part::Box] Box279  label="Cube174"
  AttacherType = Attacher::AttachEngine3D
  Height = 5
  Length = 17
  Placement = pos=(242.5,14.5,6.5) rot=(0,0,1;0rad)
  Width = 33
FEATURE [Part::Cut] Cut088
  Base = -> Cut087
  Placement = pos=(0,1,0) rot=(0,0,1;0rad)
  Tool = -> Box279
FEATURE [App::DocumentObjectGroup] Group012  label="KeyboardBezelRightBox"
  Group = -> [Cut088]
FEATURE [Part::Box] Box280  label="Cube175"
  AttacherType = Attacher::AttachEngine3D
  Height = 2
  Length = 23
  Placement = pos=(231,14,5) rot=(0,0,1;0rad)
  Width = 36
FEATURE [Part::Box] Box281  label="Cube176"
  AttacherType = Attacher::AttachEngine3D
  Height = 2
  Length = 23
  Placement = pos=(235,15.5,5) rot=(0,0,1;0rad)
  Width = 33
FEATURE [Part::Cut] Cut089
  Base = -> Box280
  Tool = -> Box281
FEATURE [Part::MultiFuse] Fusion045
  Shapes = -> [Box268,Box269,Box270,Box271,Box273,Box274,Box275,Cylinder031,Cylinder032,Box276,Box277,Cut089]
FEATURE [Part::Cut] Cut085
  Base = -> Fusion045
  Tool = -> Cylinder030
FEATURE [Part::Cut] Cut086  label="KeyboardBezelRight"
  Base = -> Cut085
  Tool = -> Cylinder029
